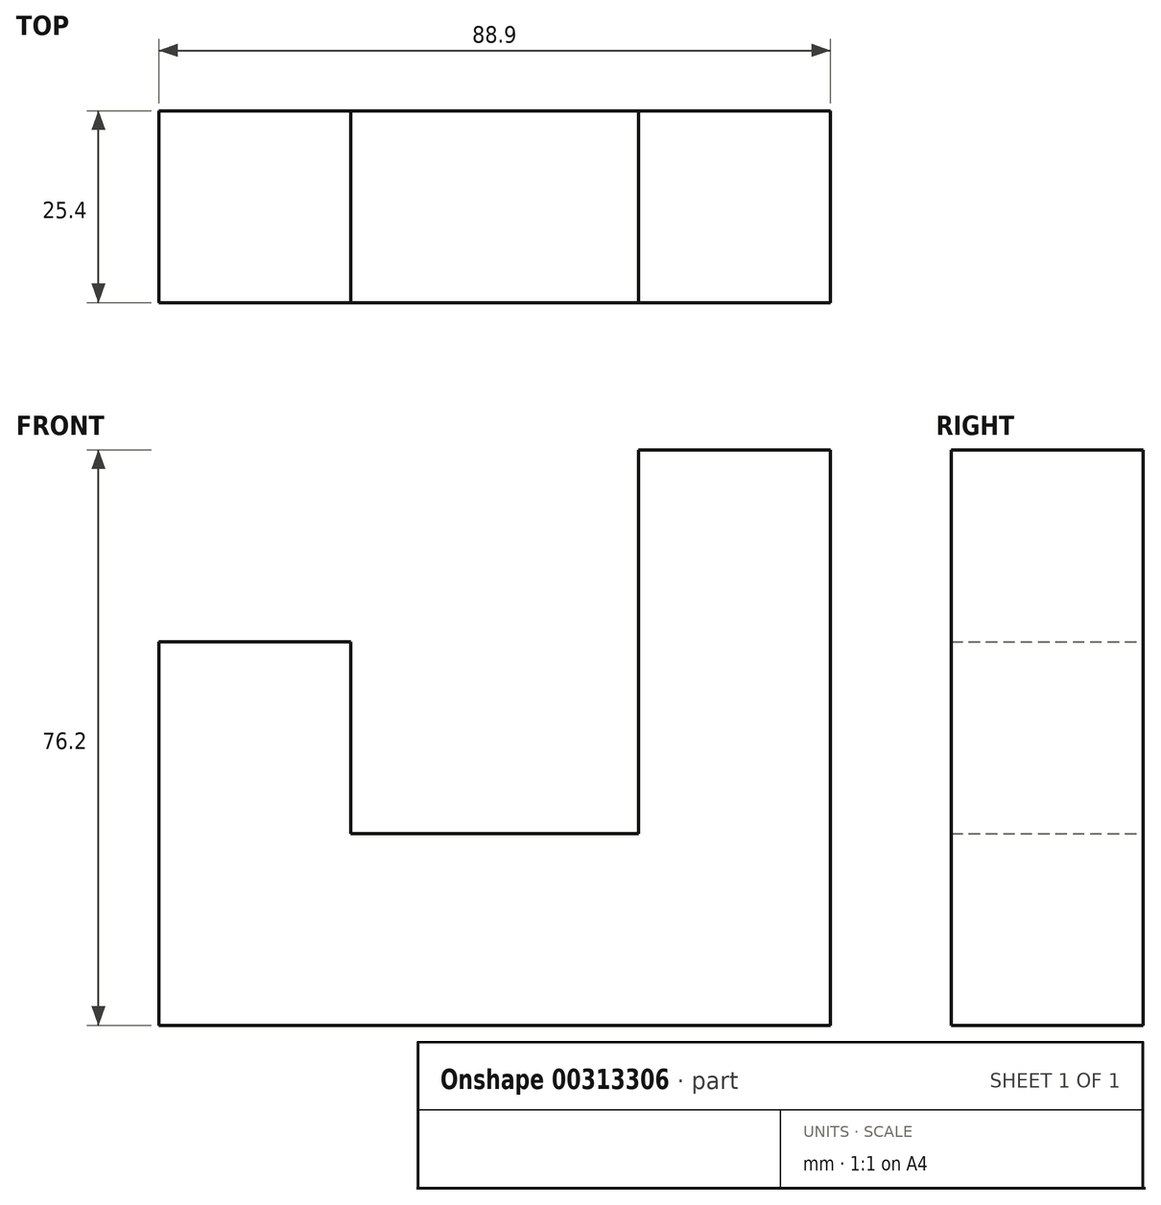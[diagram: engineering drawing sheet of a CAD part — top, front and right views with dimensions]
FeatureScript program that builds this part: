
annotation { "Feature Type Name" : "Feature", "Feature Type Description" : "" }
export const myFeature = defineFeature(function(context is Context, id is Id, definition is map)
    precondition{}
    {
        {
            var Q0;
            Q0=qCreatedBy(makeId("Front.planeOp"),FACE);
            var sketch = newSketch(context, id + "F0", { "sketchPlane" : qUnion([Q0])});
            skLineSegment(sketch, "E0", {"start": v(-41.35, -25.4) * mm, "end": v(47.55, -25.4) * mm});
            skLineSegment(sketch, "E1", {"start": v(47.55, -25.4) * mm, "end": v(47.55, 50.8) * mm});
            skLineSegment(sketch, "E2", {"start": v(47.55, 50.8) * mm, "end": v(22.15, 50.8) * mm});
            skLineSegment(sketch, "E3", {"start": v(22.15, 50.8) * mm, "end": v(22.15, 0) * mm});
            skLineSegment(sketch, "E4", {"start": v(22.15, 0) * mm, "end": v(-15.95, 0) * mm});
            skLineSegment(sketch, "E5", {"start": v(-15.95, 0) * mm, "end": v(-15.95, 25.4) * mm});
            skLineSegment(sketch, "E6", {"start": v(-15.95, 25.4) * mm, "end": v(-41.35, 25.4) * mm});
            skLineSegment(sketch, "E7", {"start": v(-41.35, 25.4) * mm, "end": v(-41.35, -25.4) * mm});
            skSolve(sketch);
        }
        {
            var Q0;
            Q0=makeQuery(id+"F0.imprint","IMPRINT",FACE,{"disambiguationData":[TD([[makeQuery(id+"F0.imprint","IMPRINT",EDGE,{"derivedFrom":sQuery(id+"F0.wireOp",EDGE,"E0")}),1.0]])]});
            extrude(context, id + "F1", {"entities" : qUnion([Q0]), "depth" : 25.4 * mm});
        }
    });
